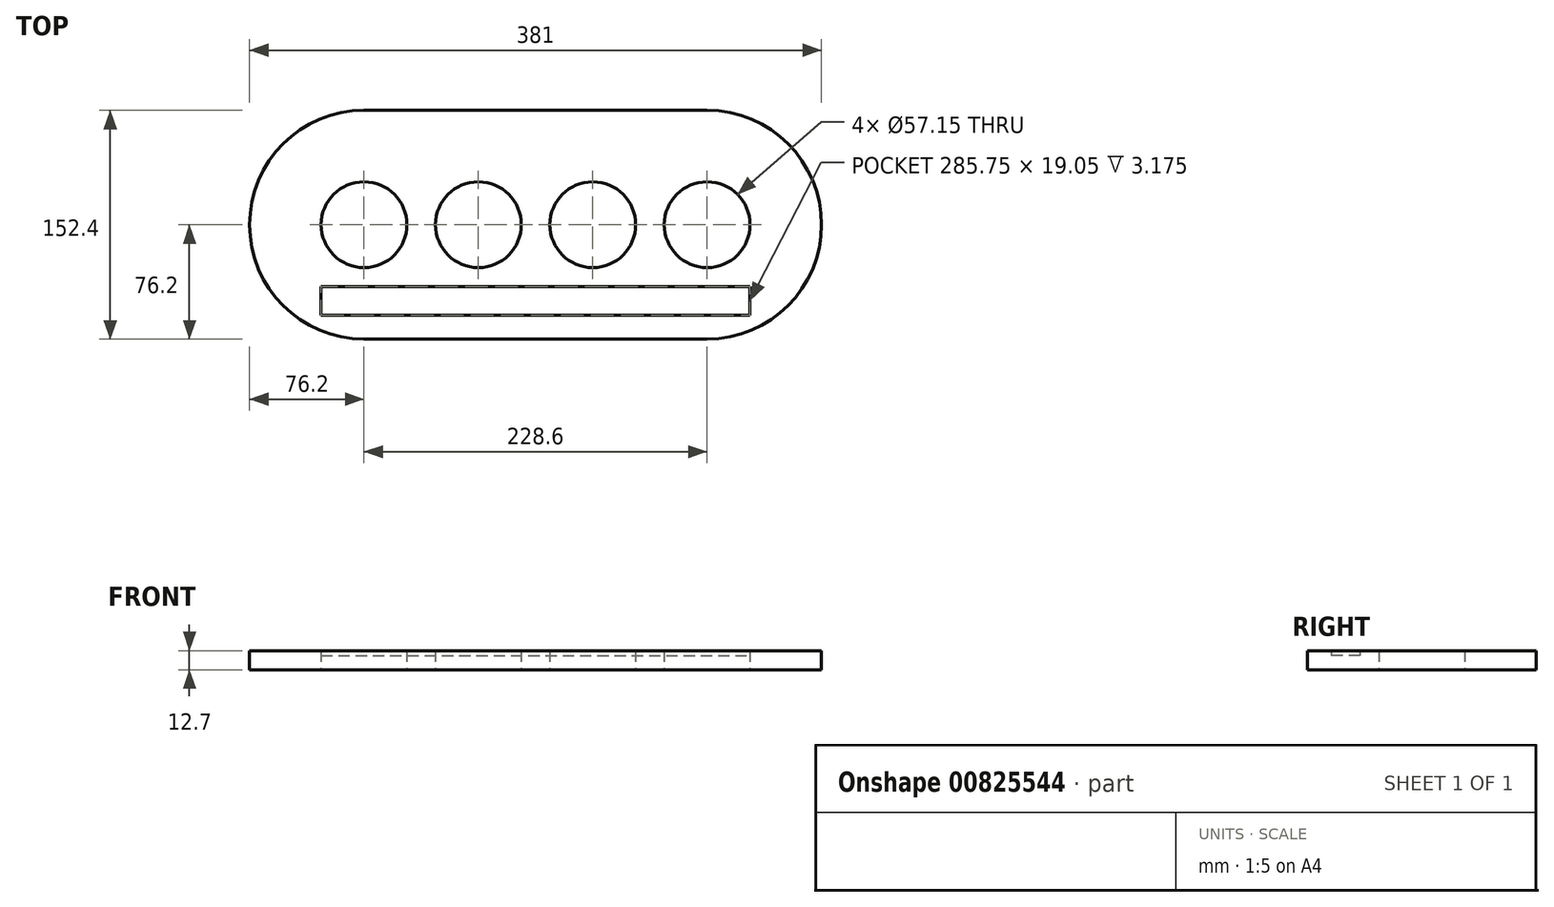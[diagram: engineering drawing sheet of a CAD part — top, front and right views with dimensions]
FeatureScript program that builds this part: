
annotation { "Feature Type Name" : "Feature", "Feature Type Description" : "" }
export const myFeature = defineFeature(function(context is Context, id is Id, definition is map)
    precondition{}
    {
        {
            var Q0;
            Q0=qCreatedBy(makeId("Top.planeOp"),FACE);
            var sketch = newSketch(context, id + "F0", { "sketchPlane" : qUnion([Q0])});
            skCircle(sketch, "E0", {"center": v(0, 0) * mm, "radius": 28.58 * mm});
            skCircle(sketch, "E1.1.0.0", {"center": v(76.2, 0) * mm, "radius": 28.58 * mm});
            skCircle(sketch, "E1.2.0.0", {"center": v(152.4, 0) * mm, "radius": 28.58 * mm});
            skCircle(sketch, "E1.3.0.0", {"center": v(228.6, 0) * mm, "radius": 28.58 * mm});
            skLineSegment(sketch, "E1.direction1", {"start": v(0, 0) * mm, "end": v(76.2, 0) * mm, "construction": true});
            skArc(sketch, "E2", {"start": v(0, 76.2) * mm, "mid": v(-76.2, 0) * mm, "end": v(0, -76.2) * mm});
            skLineSegment(sketch, "E3", {"start": v(0, 76.2) * mm, "end": v(228.6, 76.2) * mm});
            skLineSegment(sketch, "E4", {"start": v(228.6, -76.2) * mm, "end": v(0, -76.2) * mm});
            skArc(sketch, "E5.trimOffspring", {"start": v(228.6, -76.2) * mm, "mid": v(304.8, 0) * mm, "end": v(228.6, 76.2) * mm});
            skLineSegment(sketch, "E6.bottom", {"start": v(-28.57, -41.27) * mm, "end": v(257.18, -41.27) * mm});
            skLineSegment(sketch, "E6.top", {"start": v(-28.57, -60.32) * mm, "end": v(257.18, -60.32) * mm});
            skLineSegment(sketch, "E6.left", {"start": v(-28.57, -41.27) * mm, "end": v(-28.57, -60.32) * mm});
            skLineSegment(sketch, "E6.right", {"start": v(257.18, -41.27) * mm, "end": v(257.18, -60.32) * mm});
            skSolve(sketch);
        }
        {
            var Q0;
            Q0=makeQuery(id+"F0.imprint","IMPRINT",FACE,{"disambiguationData":[TD([[makeQuery(id+"F0.imprint","IMPRINT",EDGE,{"derivedFrom":sQuery(id+"F0.wireOp",EDGE,"E6.bottom")}),-1.0]])]});
            extrude(context, id + "F1", {"entities" : qUnion([Q0]), "depth" : 9.52 * mm, "offsetDistance" : 25.4 * mm});
        }
        {
            var Q0;
            Q0=qSketchRegion(id+"F0",true);
            extrude(context, id + "F2", {"entities" : qUnion([Q0]), "operationType" : NewBodyOperationType.ADD, "depth" : 12.7 * mm, "offsetDistance" : 25.4 * mm});
        }
    });
